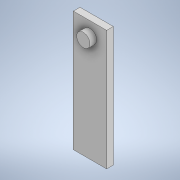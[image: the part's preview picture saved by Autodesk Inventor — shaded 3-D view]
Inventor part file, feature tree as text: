
AUTODESK INVENTOR PART (.ipt)
format: ipt  version: 2022 (Build 260153000, 153)  size: 103,424 bytes
history: native  units: mm
features: extrude x2, sketch x2, other x1
ambient origin geometry x8: Origin, YZ Plane, XZ Plane, XY Plane, X Axis, Y Axis, Z Axis, Center Point
bodies: Body1 (feature_tree)
feature tree (5):
  other  "솔리드1"
  extrude  "돌출1"  Depth=5.0mm
  extrude  "돌출2"  Depth=18.0mm
  sketch  "스케치1"
  sketch  "스케치2"
